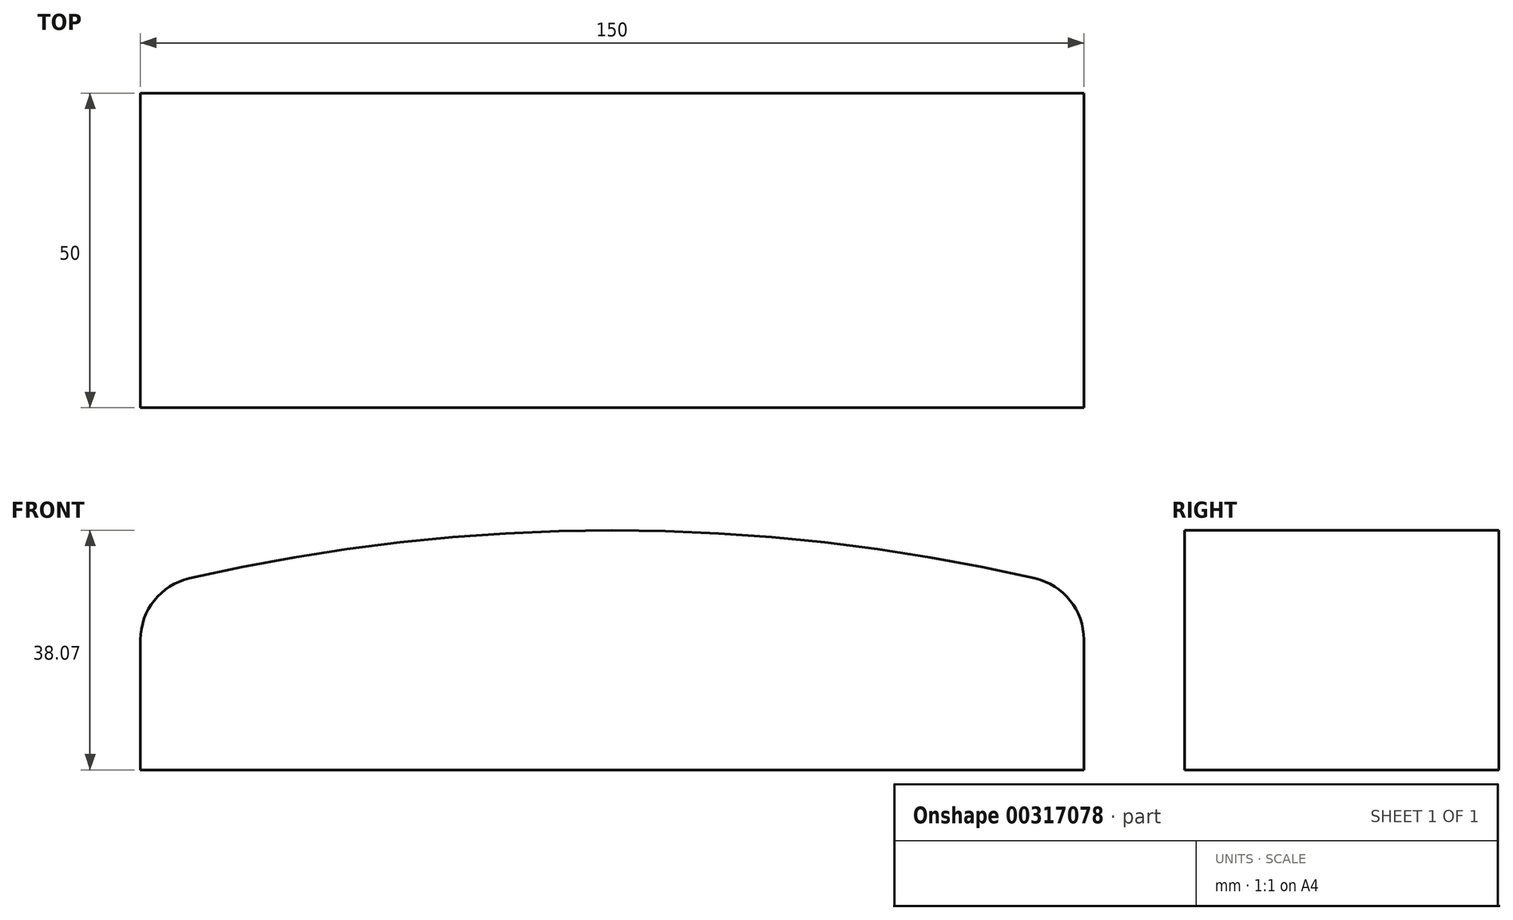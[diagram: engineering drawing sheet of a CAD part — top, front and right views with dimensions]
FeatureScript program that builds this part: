
annotation { "Feature Type Name" : "Feature", "Feature Type Description" : "" }
export const myFeature = defineFeature(function(context is Context, id is Id, definition is map)
    precondition{}
    {
        {
            var Q0;
            Q0=qCreatedBy(makeId("Front.planeOp"),FACE);
            var sketch = newSketch(context, id + "F0", { "sketchPlane" : qUnion([Q0])});
            skLineSegment(sketch, "E0.top", {"start": v(75, -14.27) * mm, "end": v(-75, -14.27) * mm});
            skLineSegment(sketch, "E0.left", {"start": v(75, 14.27) * mm, "end": v(75, -14.27) * mm});
            skLineSegment(sketch, "E0.right", {"start": v(-75, 14.27) * mm, "end": v(-75, -14.27) * mm});
            skPoint(sketch, "E0.middle", {"position": v(0, 0) * mm});
            skArc(sketch, "E1", {"start": v(75, 14.27) * mm, "mid": v(0, 23.8) * mm, "end": v(-75, 14.27) * mm});
            skLineSegment(sketch, "E2.bottom", {"start": v(-75, 0) * mm, "end": v(75, 0) * mm});
            skLineSegment(sketch, "E2.top", {"start": v(-75, 5) * mm, "end": v(75, 5) * mm});
            skLineSegment(sketch, "E2.left", {"start": v(-75, 0) * mm, "end": v(-75, 5) * mm});
            skLineSegment(sketch, "E2.right", {"start": v(75, 0) * mm, "end": v(75, 5) * mm});
            skSolve(sketch);
        }
        {
            var Q0;
            {var subQ0=sQuery(id+"F0.wireOp",EDGE,"E1");Q0=makeQuery(id+"F0.imprint","IMPRINT",FACE,{"disambiguationData":[TD([[makeQuery(id+"F0.imprint","IMPRINT",EDGE,{"derivedFrom":subQ0}),1.0]])]});}
            var Q1;
            {var subQ0=sQuery(id+"F0.wireOp",EDGE,"E0.top");Q1=makeQuery(id+"F0.imprint","IMPRINT",FACE,{"disambiguationData":[TD([[makeQuery(id+"F0.imprint","IMPRINT",EDGE,{"derivedFrom":subQ0}),-1.0]])]});}
            extrude(context, id + "F1", {"entities" : qUnion([Q0, Q1]), "depth" : 50 * mm});
        }
        {
            var Q0;
            Q0=makeQuery(id+"F1.opExtrude","SWEPT_EDGE",EDGE,{"disambiguationData":[OSD([sQuery(id+"F0.wireOp",EDGE,"E0.left"),sQuery(id+"F0.wireOp",EDGE,"E1")])]});
            var Q1;
            Q1=makeQuery(id+"F1.opExtrude","SWEPT_EDGE",EDGE,{"disambiguationData":[OSD([sQuery(id+"F0.wireOp",EDGE,"E0.right"),sQuery(id+"F0.wireOp",EDGE,"E1")])]});
            fillet(context, id + "F2", {"entities" : qUnion([Q0, Q1]), "radius" : 10 * mm, "tangentPropagation" : true, "allowEdgeOverflow" : false});
        }
        {
            var Q0;
            Q0=makeQuery(id+"F0.imprint","IMPRINT",FACE,{"disambiguationData":[TD([[makeQuery(id+"F0.imprint","IMPRINT",EDGE,{"derivedFrom":sQuery(id+"F0.wireOp",EDGE,"E2.bottom")}),1.0]])]});
            extrude(context, id + "F3", {"entities" : qUnion([Q0]), "depth" : 50 * mm});
        }
        {
            var Q0;
            Q0=makeQuery(id+"F1.opExtrude","SWEPT_FACE",FACE,{"disambiguationData":[OSD([sQuery(id+"F0.wireOp",EDGE,"E0.top")])]});
            var sketch = newSketch(context, id + "F4", { "sketchPlane" : qUnion([Q0])});
            skLineSegment(sketch, "E3.bottom", {"start": v(-71.5, 46.5) * mm, "end": v(71.5, 46.5) * mm});
            skLineSegment(sketch, "E3.top", {"start": v(-71.5, 3.5) * mm, "end": v(71.5, 3.5) * mm});
            skLineSegment(sketch, "E3.left", {"start": v(-71.5, 46.5) * mm, "end": v(-71.5, 3.5) * mm});
            skLineSegment(sketch, "E3.right", {"start": v(71.5, 46.5) * mm, "end": v(71.5, 3.5) * mm});
            skPoint(sketch, "E3.middle", {"position": v(0, 25) * mm});
            skSolve(sketch);
        }
        {
            var Q0;
            Q0=makeQuery(id+"F4.imprint","IMPRINT",FACE,{"disambiguationData":[TD([[makeQuery(id+"F4.imprint","IMPRINT",EDGE,{"derivedFrom":sQuery(id+"F4.wireOp",EDGE,"E3.bottom")}),-1.0]])]});
            extrude(context, id + "F5", {"entities" : qUnion([Q0]), "operationType" : NewBodyOperationType.ADD, "oppositeDirection" : true, "depth" : 19.27 * mm});
        }
    });
